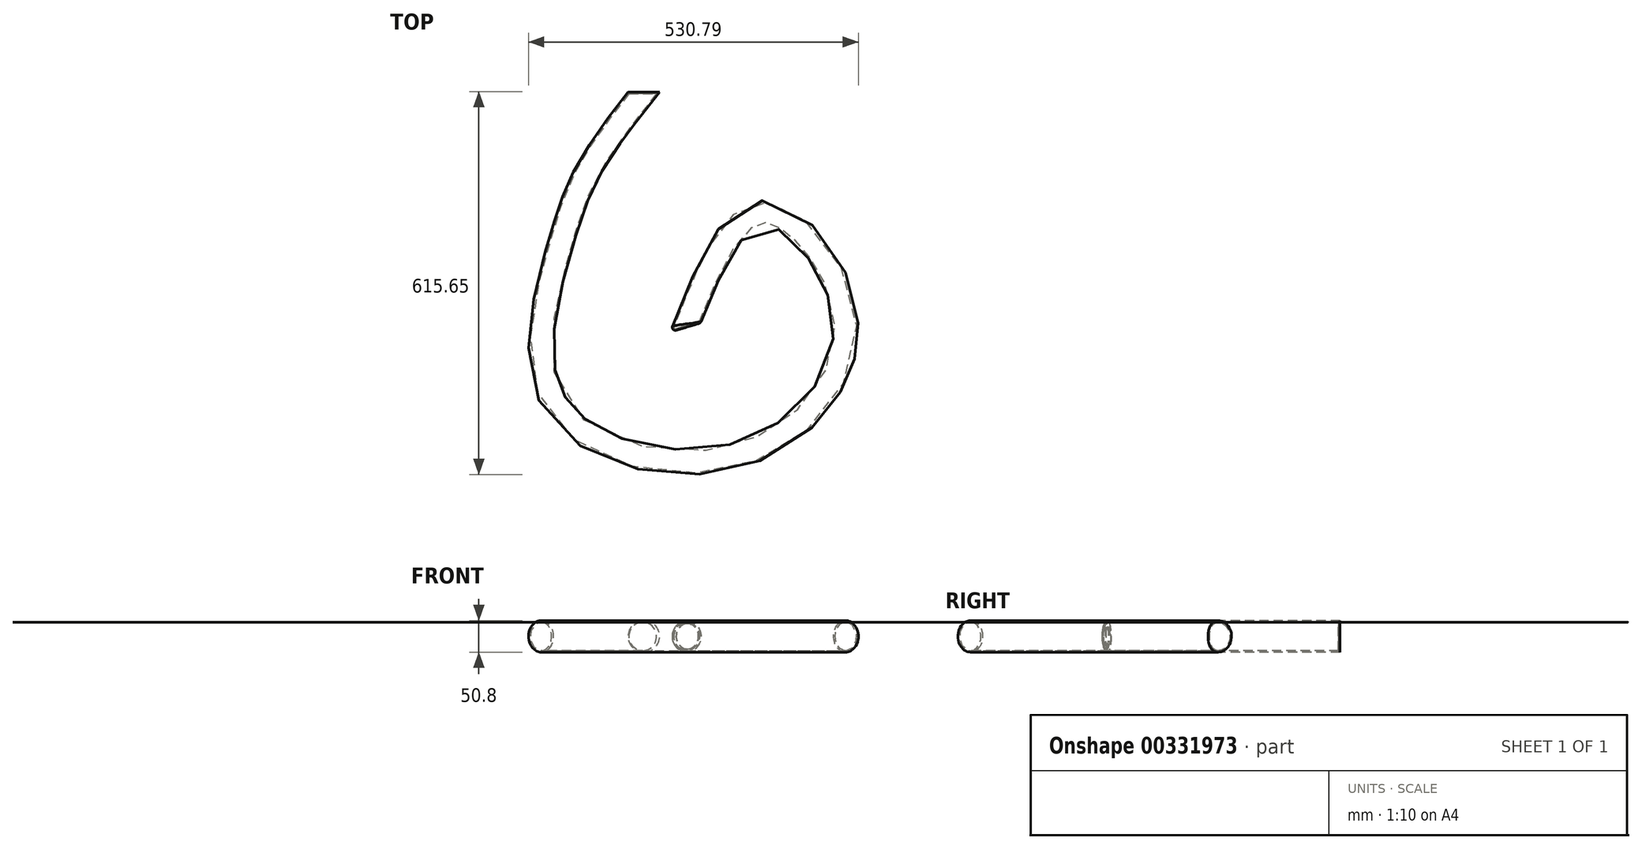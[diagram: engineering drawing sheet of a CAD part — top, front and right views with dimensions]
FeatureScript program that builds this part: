
annotation { "Feature Type Name" : "Feature", "Feature Type Description" : "" }
export const myFeature = defineFeature(function(context is Context, id is Id, definition is map)
    precondition{}
    {
        {
            var Q0;
            Q0=qCreatedBy(makeId("Front.planeOp"),FACE);
            var sketch = newSketch(context, id + "F0", { "sketchPlane" : qUnion([Q0])});
            skCircle(sketch, "E0", {"center": v(0, 0) * mm, "radius": 25.4 * mm});
            skSolve(sketch);
        }
        {
            var Q0;
            Q0=qCreatedBy(makeId("Top.planeOp"),FACE);
            var sketch = newSketch(context, id + "F1", { "sketchPlane" : qUnion([Q0])});
            skFitSpline(sketch, "E1", {"points": [v(0, 0) * mm, v(-88.1, -123.92) * mm, v(-135.72, -250.54) * mm, v(-141.96, -502.35) * mm, v(156.62, -582.14) * mm, v(323.93, -365.93) * mm, v(192.66, -196.04) * mm, v(66.53, -378.8) * mm], "startDerivative": vector(-831.03, -1059.77) * mm, "endDerivative": vector(-749.4, -1897.34) * mm});
            skSolve(sketch);
        }
        {
            var Q0;
            Q0=makeQuery(id+"F0.imprint","IMPRINT",FACE,{"disambiguationData":[TD([[makeQuery(id+"F0.imprint","IMPRINT",EDGE,{"derivedFrom":sQuery(id+"F0.wireOp",EDGE,"E0")}),1.0]])]});
            var Q1;
            Q1=sQuery(id+"F1.wireOp",EDGE,"E1");
            sweep(context, id + "F2", {"profiles" : qUnion([Q0]), "path" : qUnion([Q1])});
        }
        {
            var Q0;
            Q0=makeQuery(id+"F2.opSweep","CAP_EDGE",EDGE,{"disambiguationData":[OSD([sQuery(id+"F0.wireOp",EDGE,"E0"),sQuery(id+"F1.wireOp",VERTEX,"E1.end")])],"isStart":false});
            fillet(context, id + "F3", {"entities" : qUnion([Q0]), "radius" : 5.08 * mm, "tangentPropagation" : true, "allowEdgeOverflow" : false});
        }
        {
            var Q0;
            Q0=makeQuery(id+"F2.opSweep","CAP_FACE",FACE,{"disambiguationData":[OSD([sQuery(id+"F0.wireOp",EDGE,"E0"),sQuery(id+"F1.wireOp",VERTEX,"E1.end")])],"isStart":false});
            shell(context, id + "F4", {"entities" : qUnion([Q0]), "thickness" : 2.54 * mm});
        }
    });
